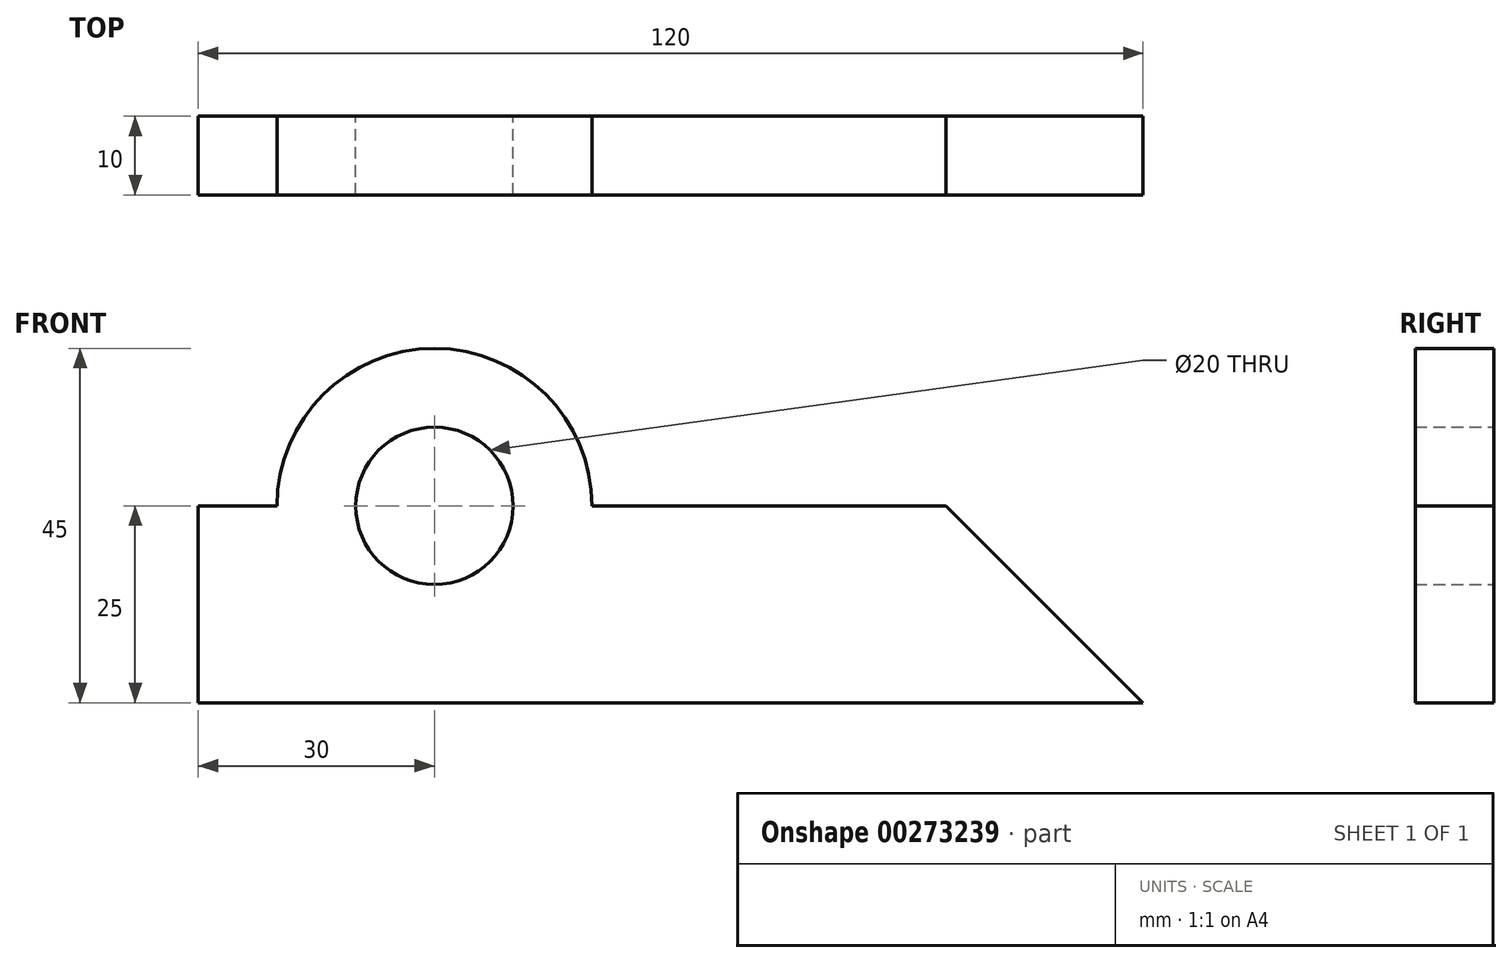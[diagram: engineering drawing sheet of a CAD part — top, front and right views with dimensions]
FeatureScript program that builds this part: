
annotation { "Feature Type Name" : "Feature", "Feature Type Description" : "" }
export const myFeature = defineFeature(function(context is Context, id is Id, definition is map)
    precondition{}
    {
        {
            var Q0;
            Q0=qCreatedBy(makeId("Front.planeOp"),FACE);
            var sketch = newSketch(context, id + "F0", { "sketchPlane" : qUnion([Q0])});
            skLineSegment(sketch, "E0", {"start": v(0, 0) * mm, "end": v(0, 25) * mm});
            skLineSegment(sketch, "E1", {"start": v(0, 0) * mm, "end": v(120, 0) * mm});
            skLineSegment(sketch, "E2", {"start": v(120, 0) * mm, "end": v(95, 25) * mm});
            skCircle(sketch, "E3", {"center": v(30, 25) * mm, "radius": 10 * mm});
            skArc(sketch, "E4", {"start": v(50, 25) * mm, "mid": v(30, 45) * mm, "end": v(10, 25) * mm});
            skLineSegment(sketch, "E5", {"start": v(0, 25) * mm, "end": v(10, 25) * mm});
            skLineSegment(sketch, "E6", {"start": v(95, 25) * mm, "end": v(50, 25) * mm});
            skSolve(sketch);
        }
        {
            var Q0;
            Q0 = qSketchRegion(id + "F0", true);
            extrude(context, id + "F1", {"entities" : qUnion([Q0]), "depth" : 10 * mm});
        }
    });
